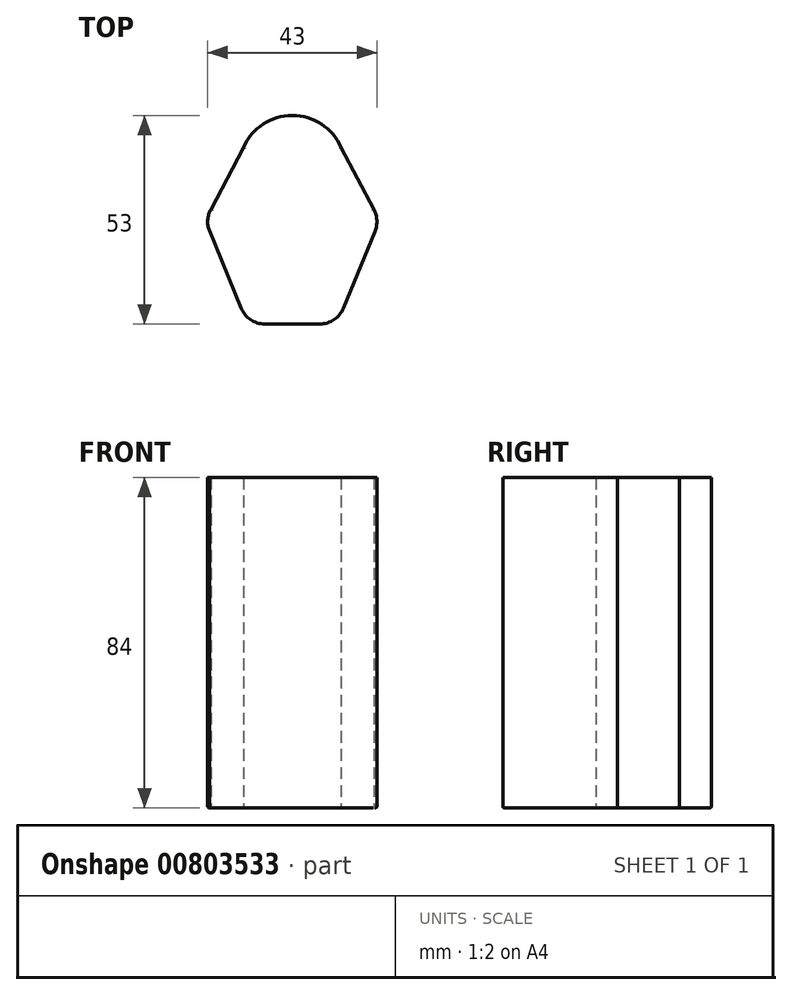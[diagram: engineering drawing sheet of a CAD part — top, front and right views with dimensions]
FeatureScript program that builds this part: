
annotation { "Feature Type Name" : "Feature", "Feature Type Description" : "" }
export const myFeature = defineFeature(function(context is Context, id is Id, definition is map)
    precondition{}
    {
        {
            var Q0;
            Q0=qCreatedBy(makeId("Top.planeOp"),FACE);
            var sketch = newSketch(context, id + "F0", { "sketchPlane" : qUnion([Q0])});
            skArc(sketch, "E0", {"start": v(12.4, 20.62) * mm, "mid": v(0, 28.79) * mm, "end": v(-12.4, 20.62) * mm});
            skLineSegment(sketch, "E1", {"start": v(-7, -24.21) * mm, "end": v(7, -24.21) * mm});
            skArc(sketch, "E2", {"start": v(-20.7, 4.91) * mm, "mid": v(-21.48, 2.23) * mm, "end": v(-21.07, -0.53) * mm});
            skArc(sketch, "E3", {"start": v(21.01, -0.69) * mm, "mid": v(21.49, 2.15) * mm, "end": v(20.7, 4.91) * mm});
            skArc(sketch, "E4", {"start": v(-13.01, -20.18) * mm, "mid": v(-10.62, -23.11) * mm, "end": v(-7, -24.21) * mm});
            skArc(sketch, "E5", {"start": v(7, -24.21) * mm, "mid": v(10.62, -23.11) * mm, "end": v(13.02, -20.18) * mm});
            skLineSegment(sketch, "E6", {"start": v(-21.07, -0.53) * mm, "end": v(-13.01, -20.18) * mm});
            skLineSegment(sketch, "E7", {"start": v(13.02, -20.18) * mm, "end": v(21.01, -0.69) * mm});
            skLineSegment(sketch, "E8", {"start": v(-20.7, 4.91) * mm, "end": v(-12.4, 20.62) * mm});
            skLineSegment(sketch, "E9", {"start": v(12.4, 20.62) * mm, "end": v(20.7, 4.91) * mm});
            skPoint(sketch, "E10.orphan", {"position": v(-7, 15.29) * mm});
            skPoint(sketch, "E11.start.orphan", {"position": v(0, 28.79) * mm});
            skPoint(sketch, "E12.orphan", {"position": v(7, 15.29) * mm});
            skSolve(sketch);
        }
        {
            var Q0;
            Q0=qSketchRegion(id+"F0",true);
            extrude(context, id + "F1", {"entities" : qUnion([Q0]), "depth" : 84 * mm, "offsetDistance" : 25 * mm});
        }
        {
            var Q0;
            Q0=makeQuery(id+"F1.opExtrude","CAP_EDGE",EDGE,{"disambiguationData":[OSD([sQuery(id+"F0.wireOp",EDGE,"E0")])],"isStart":true});
            var Q1;
            Q1=makeQuery(id+"F1.opExtrude","CAP_EDGE",EDGE,{"disambiguationData":[OSD([sQuery(id+"F0.wireOp",EDGE,"E8")])],"isStart":true});
            var Q2;
            Q2=makeQuery(id+"F1.opExtrude","CAP_EDGE",EDGE,{"disambiguationData":[OSD([sQuery(id+"F0.wireOp",EDGE,"E2")])],"isStart":true});
            var Q3;
            Q3=makeQuery(id+"F1.opExtrude","CAP_EDGE",EDGE,{"disambiguationData":[OSD([sQuery(id+"F0.wireOp",EDGE,"E6")])],"isStart":true});
            var Q4;
            Q4=makeQuery(id+"F1.opExtrude","CAP_EDGE",EDGE,{"disambiguationData":[OSD([sQuery(id+"F0.wireOp",EDGE,"E4")])],"isStart":true});
            var Q5;
            Q5=makeQuery(id+"F1.opExtrude","CAP_EDGE",EDGE,{"disambiguationData":[OSD([sQuery(id+"F0.wireOp",EDGE,"E1")])],"isStart":true});
            var Q6;
            Q6=makeQuery(id+"F1.opExtrude","CAP_EDGE",EDGE,{"disambiguationData":[OSD([sQuery(id+"F0.wireOp",EDGE,"E5")])],"isStart":true});
            var Q7;
            Q7=makeQuery(id+"F1.opExtrude","CAP_EDGE",EDGE,{"disambiguationData":[OSD([sQuery(id+"F0.wireOp",EDGE,"E7")])],"isStart":true});
            var Q8;
            Q8=makeQuery(id+"F1.opExtrude","CAP_EDGE",EDGE,{"disambiguationData":[OSD([sQuery(id+"F0.wireOp",EDGE,"E3")])],"isStart":true});
            var Q9;
            Q9=makeQuery(id+"F1.opExtrude","CAP_EDGE",EDGE,{"disambiguationData":[OSD([sQuery(id+"F0.wireOp",EDGE,"E9")])],"isStart":true});
            fillet(context, id + "F2", {"entities" : qUnion([Q0, Q1, Q2, Q3, Q4, Q5, Q6, Q7, Q8, Q9]), "radius" : .5 * mm, "tangentPropagation" : true, "allowEdgeOverflow" : false});
        }
    });
